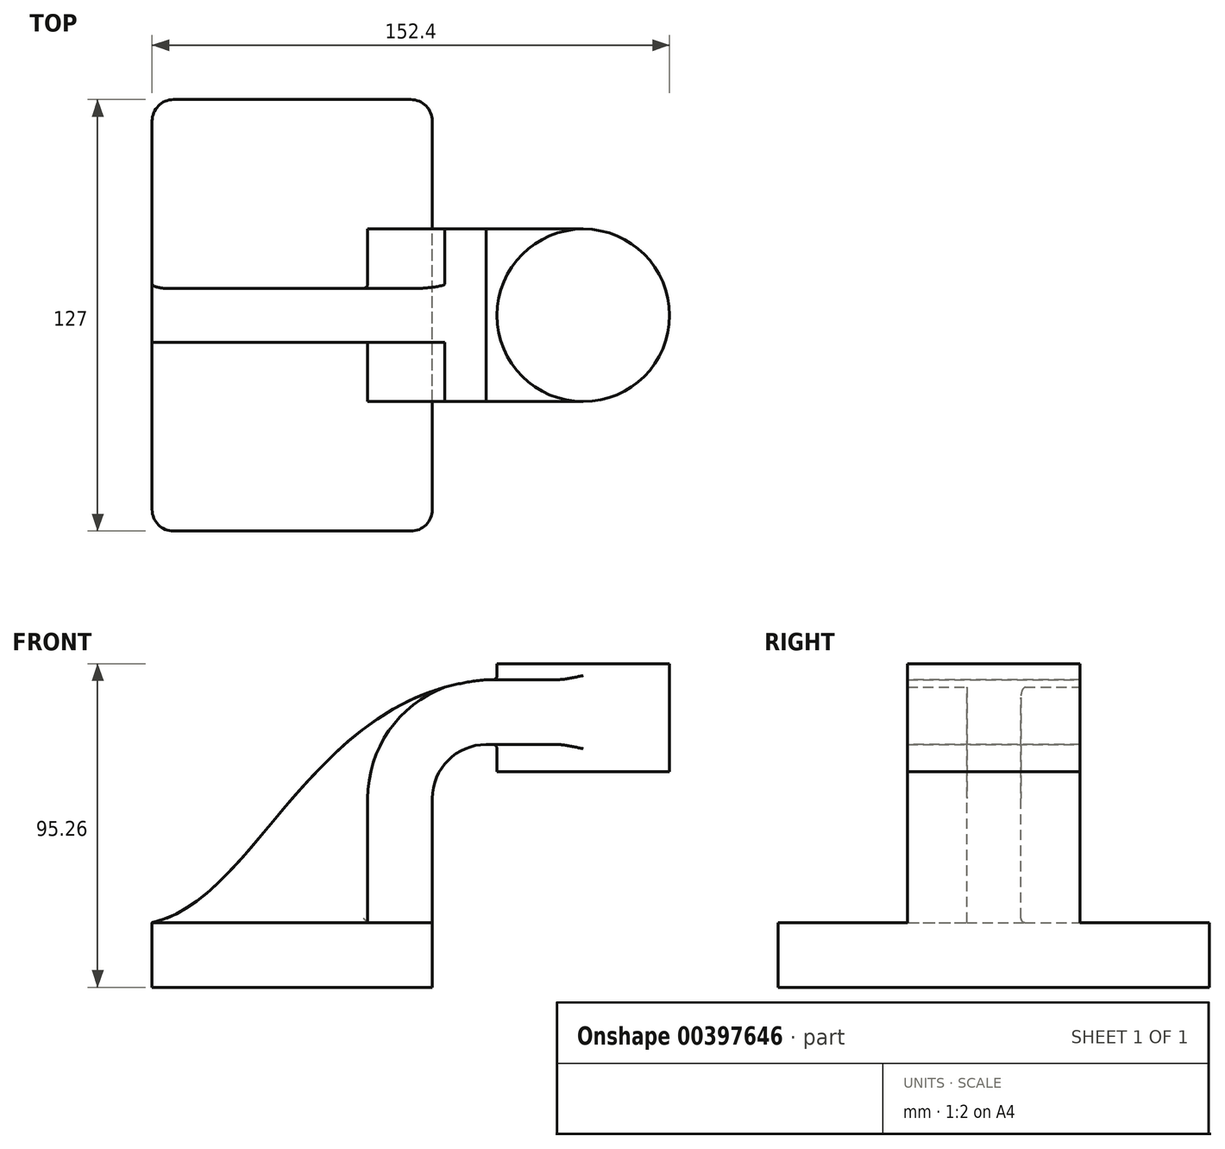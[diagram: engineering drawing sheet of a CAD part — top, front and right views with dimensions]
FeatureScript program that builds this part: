
annotation { "Feature Type Name" : "Feature", "Feature Type Description" : "" }
export const myFeature = defineFeature(function(context is Context, id is Id, definition is map)
    precondition{}
    {
        {
            var Q0;
            Q0=qCreatedBy(makeId("Front.planeOp"),FACE);
            var sketch = newSketch(context, id + "F0", { "sketchPlane" : qUnion([Q0])});
            skLineSegment(sketch, "E0.bottom", {"start": v(41.22, -9.53) * mm, "end": v(-41.33, -9.52) * mm});
            skLineSegment(sketch, "E0.top", {"start": v(41.22, 9.52) * mm, "end": v(-41.33, 9.53) * mm});
            skLineSegment(sketch, "E0.left", {"start": v(41.22, -9.53) * mm, "end": v(41.22, 9.53) * mm});
            skLineSegment(sketch, "E0.right", {"start": v(-41.33, -9.53) * mm, "end": v(-41.33, 9.53) * mm});
            skPoint(sketch, "E0.middle", {"position": v(-0.05, 0) * mm});
            skLineSegment(sketch, "E1.bottom", {"start": v(60.27, 53.98) * mm, "end": v(111.07, 53.98) * mm});
            skLineSegment(sketch, "E1.top", {"start": v(60.27, 85.73) * mm, "end": v(111.07, 85.73) * mm});
            skLineSegment(sketch, "E1.left", {"start": v(60.27, 53.98) * mm, "end": v(60.27, 85.72) * mm});
            skLineSegment(sketch, "E1.right", {"start": v(111.07, 53.98) * mm, "end": v(111.07, 85.72) * mm});
            skPoint(sketch, "E1.middle", {"position": v(85.67, 69.85) * mm});
            skLineSegment(sketch, "E2", {"start": v(41.22, 9.53) * mm, "end": v(41.22, 46.05) * mm});
            skArc(sketch, "E3", {"start": v(41.22, 46.05) * mm, "mid": v(45.87, 57.28) * mm, "end": v(57.1, 61.93) * mm});
            skArc(sketch, "E4.1", {"start": v(22.17, 46.05) * mm, "mid": v(32.4, 70.75) * mm, "end": v(57.1, 80.98) * mm});
            skLineSegment(sketch, "E4.2", {"start": v(22.17, 9.52) * mm, "end": v(22.17, 46.05) * mm});
            skFitSpline(sketch, "E5", {"points": [v(-41.33, 9.53) * mm, v(57.1, 80.98) * mm], "startDerivative": vector(92.66, 19.7) * mm, "endDerivative": vector(155.64, 13.31) * mm});
            skLineSegment(sketch, "E6", {"start": v(57.1, 80.98) * mm, "end": v(85.67, 80.98) * mm});
            skLineSegment(sketch, "E7", {"start": v(57.1, 61.93) * mm, "end": v(85.67, 61.93) * mm});
            skLineSegment(sketch, "E8", {"start": v(85.67, 53.98) * mm, "end": v(85.67, 85.73) * mm});
            skSolve(sketch);
        }
        {
            var Q0;
            Q0=makeQuery(id+"F0.imprint","IMPRINT",FACE,{"disambiguationData":[TD([[makeQuery(id+"F0.imprint","IMPRINT",EDGE,{"derivedFrom":sQuery(id+"F0.wireOp",EDGE,"E0.bottom")}),-1.0]])]});
            extrude(context, id + "F1", {"entities" : qUnion([Q0]), "endBound" : BoundingType.SYMMETRIC, "depth" : 127 * mm});
        }
        {
            var Q0;
            {var subQ1=sQuery(id+"F0.wireOp",EDGE,"E2");Q0=makeQuery(id+"F0.imprint","IMPRINT",FACE,{"disambiguationData":[TD([[makeQuery(id+"F0.imprint","IMPRINT",EDGE,{"derivedFrom":subQ1}),1.0]])]});}
            var Q1;
            {var subQ0=sQuery(id+"F0.wireOp",EDGE,"E7");var subQ1=sQuery(id+"F0.wireOp",EDGE,"E1.left");var subQ2=makeQuery(id+"F0.imprint","INTERSECT",VERTEX,{"derivedFrom":[subQ1,subQ0]});Q1=makeQuery(id+"F0.imprint","IMPRINT",FACE,{"disambiguationData":[TD([[makeQuery(id+"F0.imprint","IMPRINT",EDGE,{"disambiguationData":[TD([[subQ2,-1.0]])],"derivedFrom":subQ1}),-1.0]])]});}
            extrude(context, id + "F2", {"entities" : qUnion([Q0, Q1]), "operationType" : NewBodyOperationType.ADD, "endBound" : BoundingType.SYMMETRIC, "depth" : 50.8 * mm});
        }
        {
            var Q0;
            {var subQ3=sQuery(id+"F0.wireOp",EDGE,"E4.2");Q0=makeQuery(id+"F0.imprint","IMPRINT",FACE,{"disambiguationData":[TD([[makeQuery(id+"F0.imprint","IMPRINT",EDGE,{"derivedFrom":subQ3}),1.0]])]});}
            extrude(context, id + "F3", {"entities" : qUnion([Q0]), "operationType" : NewBodyOperationType.ADD, "endBound" : BoundingType.SYMMETRIC, "depth" : 15.88 * mm});
        }
        {
            var Q0;
            {var subQ4=sQuery(id+"F0.wireOp",EDGE,"E1.right");Q0=makeQuery(id+"F0.imprint","IMPRINT",FACE,{"disambiguationData":[TD([[makeQuery(id+"F0.imprint","IMPRINT",EDGE,{"derivedFrom":subQ4}),1.0]])]});}
            var Q1;
            Q1=sQuery(id+"F0.wireOp",EDGE,"E8");
            revolve(context, id + "F4", {"operationType" : NewBodyOperationType.ADD, "entities" : qUnion([Q0]), "axis" : qUnion([Q1]), "revolveType" : RevolveType.FULL});
        }
        {
            var Q0;
            Q0=makeQuery(id+"F1.opExtrude","CAP_EDGE",EDGE,{"disambiguationData":[OSD([sQuery(id+"F0.wireOp",EDGE,"E0.right")])],"isStart":true});
            var Q1;
            Q1=makeQuery(id+"F1.opExtrude","CAP_EDGE",EDGE,{"disambiguationData":[OSD([sQuery(id+"F0.wireOp",EDGE,"E0.right")])],"isStart":false});
            var Q2;
            Q2=makeQuery(id+"F1.opExtrude","CAP_EDGE",EDGE,{"disambiguationData":[OSD([sQuery(id+"F0.wireOp",EDGE,"E0.left")])],"isStart":false});
            var Q3;
            Q3=makeQuery(id+"F1.opExtrude","CAP_EDGE",EDGE,{"disambiguationData":[OSD([sQuery(id+"F0.wireOp",EDGE,"E0.left")])],"isStart":true});
            fillet(context, id + "F5", {"entities" : qUnion([Q0, Q1, Q2, Q3]), "radius" : 6.35 * mm, "tangentPropagation" : true, "allowEdgeOverflow" : false});
        }
        {
            var Q0;
            Q0=makeQuery(id+"F4.boolean.opBoolean","INTERSECT",EDGE,{"derivedFrom":[makeQuery(id+"F2.opExtrude","SWEPT_FACE",FACE,{"disambiguationData":[OSD([sQuery(id+"F0.wireOp",EDGE,"E6")])]}),makeQuery(id+"F4.opRevolve","SWEPT_FACE",FACE,{"disambiguationData":[OSD([sQuery(id+"F0.wireOp",EDGE,"E1.right")])]})]});
            var Q1;
            Q1=makeQuery(id+"F3.opExtrude","CAP_EDGE",EDGE,{"disambiguationData":[OSD([sQuery(id+"F0.wireOp",EDGE,"E4.1")])],"isStart":false});
            var Q2;
            Q2=makeQuery(id+"F3.opExtrude","CAP_EDGE",EDGE,{"disambiguationData":[OSD([sQuery(id+"F0.wireOp",EDGE,"E4.1")])],"isStart":true});
            var Q3;
            Q3=makeQuery(id+"F3.opExtrude","CAP_EDGE",EDGE,{"disambiguationData":[OSD([sQuery(id+"F0.wireOp",EDGE,"E0.top")])],"isStart":true});
            var Q4;
            {var subQ0=sQuery(id+"F0.wireOp",EDGE,"E0.top");var subQ1=sQuery(id+"F0.wireOp",EDGE,"E5");var subQ2=sQuery(id+"F0.wireOp",EDGE,"E4.2");var subQ3=sQuery(id+"F0.wireOp",EDGE,"E4.1");Q4=makeQuery(id+"F3.boolean.opBoolean","SPLIT",EDGE,{"disambiguationData":[TD([makeQuery(id+"F3.opExtrude","CAP_FACE",FACE,{"disambiguationData":[OSD([subQ0,subQ3,subQ2,subQ1])],"isStart":true})])],"derivedFrom":makeQuery(id+"F2.opExtrude","SWEPT_EDGE",EDGE,{"disambiguationData":[OSD([subQ0,subQ2])]})});}
            var Q5;
            Q5=makeQuery(id+"F2.opExtrude","CAP_EDGE",EDGE,{"disambiguationData":[OSD([sQuery(id+"F0.wireOp",EDGE,"E0.top")])],"isStart":true});
            var Q6;
            Q6=makeQuery(id+"F3.opExtrude","CAP_EDGE",EDGE,{"disambiguationData":[OSD([sQuery(id+"F0.wireOp",EDGE,"E0.top")])],"isStart":false});
            var Q7;
            Q7=makeQuery(id+"F2.opExtrude","CAP_EDGE",EDGE,{"disambiguationData":[OSD([sQuery(id+"F0.wireOp",EDGE,"E0.top")])],"isStart":false});
            var Q8;
            {var subQ0=sQuery(id+"F0.wireOp",EDGE,"E0.top");var subQ1=sQuery(id+"F0.wireOp",EDGE,"E5");var subQ2=sQuery(id+"F0.wireOp",EDGE,"E4.2");var subQ3=sQuery(id+"F0.wireOp",EDGE,"E4.1");Q8=makeQuery(id+"F3.boolean.opBoolean","SPLIT",EDGE,{"disambiguationData":[TD([makeQuery(id+"F3.opExtrude","CAP_FACE",FACE,{"disambiguationData":[OSD([subQ0,subQ3,subQ2,subQ1])],"isStart":false})])],"derivedFrom":makeQuery(id+"F2.opExtrude","SWEPT_EDGE",EDGE,{"disambiguationData":[OSD([subQ0,subQ2])]})});}
            var Q9;
            Q9=makeQuery(id+"F4.boolean.opBoolean","INTERSECT",EDGE,{"derivedFrom":[makeQuery(id+"F2.opExtrude","SWEPT_FACE",FACE,{"disambiguationData":[OSD([sQuery(id+"F0.wireOp",EDGE,"E7")])]}),makeQuery(id+"F4.opRevolve","SWEPT_FACE",FACE,{"disambiguationData":[OSD([sQuery(id+"F0.wireOp",EDGE,"E1.right")])]})]});
            fillet(context, id + "F6", {"entities" : qUnion([Q0, Q1, Q2, Q3, Q4, Q5, Q6, Q7, Q8, Q9]), "radius" : 1.27 * mm, "tangentPropagation" : true, "allowEdgeOverflow" : false});
        }
    });
